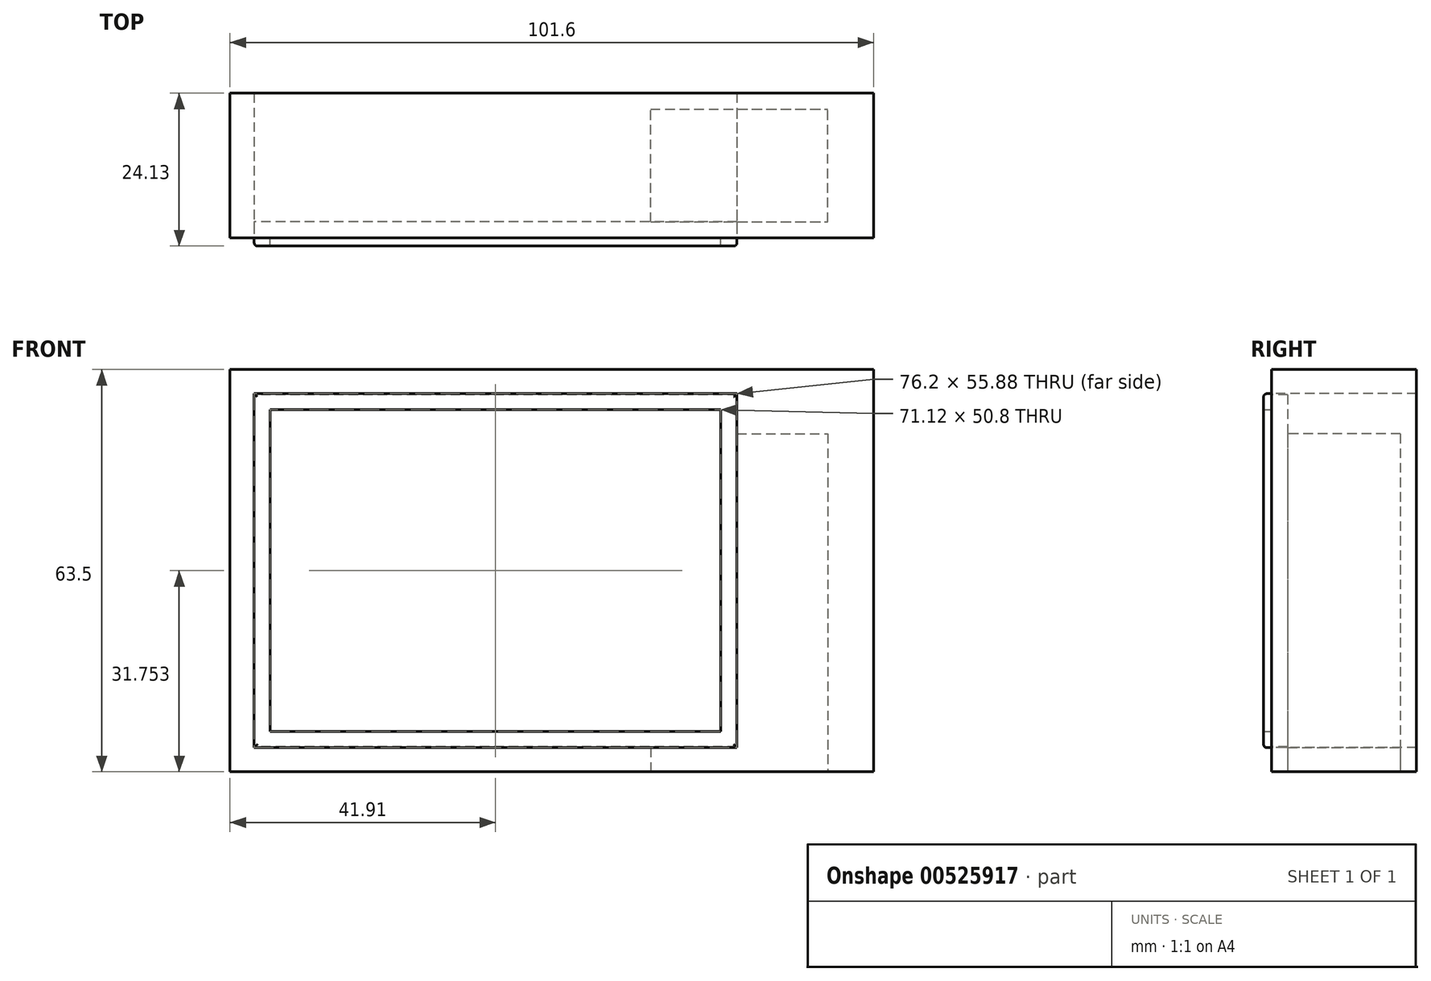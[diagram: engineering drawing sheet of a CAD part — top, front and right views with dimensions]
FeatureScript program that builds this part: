
annotation { "Feature Type Name" : "Feature", "Feature Type Description" : "" }
export const myFeature = defineFeature(function(context is Context, id is Id, definition is map)
    precondition{}
    {
        {
            var Q0;
            Q0=qCreatedBy(makeId("Front.planeOp"),FACE);
            var sketch = newSketch(context, id + "F0", { "sketchPlane" : qUnion([Q0])});
            skLineSegment(sketch, "E0.bottom", {"start": v(-51.46, 25.97) * mm, "end": v(50.14, 25.97) * mm});
            skLineSegment(sketch, "E0.top", {"start": v(-51.46, -37.53) * mm, "end": v(50.14, -37.53) * mm});
            skLineSegment(sketch, "E0.left", {"start": v(-51.46, 25.97) * mm, "end": v(-51.46, -37.53) * mm});
            skLineSegment(sketch, "E0.right", {"start": v(50.14, 25.97) * mm, "end": v(50.14, -37.53) * mm});
            skLineSegment(sketch, "E1.bottom", {"start": v(-47.65, 22.16) * mm, "end": v(28.55, 22.16) * mm});
            skLineSegment(sketch, "E1.top", {"start": v(-47.65, -33.72) * mm, "end": v(28.55, -33.72) * mm});
            skLineSegment(sketch, "E1.left", {"start": v(-47.65, 22.16) * mm, "end": v(-47.65, -33.72) * mm});
            skLineSegment(sketch, "E1.right", {"start": v(28.55, 22.16) * mm, "end": v(28.55, -33.72) * mm});
            skLineSegment(sketch, "E2.bottom", {"start": v(-45.11, 19.62) * mm, "end": v(26, 19.62) * mm});
            skLineSegment(sketch, "E2.top", {"start": v(-45.11, -31.18) * mm, "end": v(26, -31.18) * mm});
            skLineSegment(sketch, "E2.left", {"start": v(-45.11, 19.62) * mm, "end": v(-45.11, -31.18) * mm});
            skLineSegment(sketch, "E2.right", {"start": v(26, 19.62) * mm, "end": v(26, -31.18) * mm});
            skSolve(sketch);
        }
        {
            var Q0;
            Q0=makeQuery(id+"F0.imprint","IMPRINT",FACE,{"disambiguationData":[TD([[makeQuery(id+"F0.imprint","IMPRINT",EDGE,{"derivedFrom":sQuery(id+"F0.wireOp",EDGE,"E1.bottom")}),-1.0]])]});
            extrude(context, id + "F1", {"entities" : qUnion([Q0]), "depth" : 1.27 * mm, "offsetDistance" : 25.4 * mm});
        }
        {
            var Q0;
            Q0=makeQuery(id+"F1.opExtrude","CAP_EDGE",EDGE,{"disambiguationData":[OSD([sQuery(id+"F0.wireOp",EDGE,"E1.right")])],"isStart":false});
            var Q1;
            Q1=makeQuery(id+"F1.opExtrude","CAP_EDGE",EDGE,{"disambiguationData":[OSD([sQuery(id+"F0.wireOp",EDGE,"E1.bottom")])],"isStart":false});
            var Q2;
            Q2=makeQuery(id+"F1.opExtrude","CAP_EDGE",EDGE,{"disambiguationData":[OSD([sQuery(id+"F0.wireOp",EDGE,"E1.top")])],"isStart":false});
            var Q3;
            Q3=makeQuery(id+"F1.opExtrude","CAP_EDGE",EDGE,{"disambiguationData":[OSD([sQuery(id+"F0.wireOp",EDGE,"E1.left")])],"isStart":false});
            fillet(context, id + "F2", {"entities" : qUnion([Q0, Q1, Q2, Q3]), "radius" : 0.5 * mm, "tangentPropagation" : true, "allowEdgeOverflow" : false});
        }
        {
            var Q0;
            Q0=makeQuery(id+"F0.imprint","IMPRINT",FACE,{"disambiguationData":[TD([[makeQuery(id+"F0.imprint","IMPRINT",EDGE,{"derivedFrom":sQuery(id+"F0.wireOp",EDGE,"E0.bottom")}),-1.0]])]});
            extrude(context, id + "F3", {"entities" : qUnion([Q0]), "oppositeDirection" : true, "depth" : 22.86 * mm, "offsetDistance" : 25.4 * mm});
        }
        {
            var Q0;
            Q0=makeQuery(id+"F0.imprint","IMPRINT",FACE,{"disambiguationData":[TD([[makeQuery(id+"F0.imprint","IMPRINT",EDGE,{"derivedFrom":sQuery(id+"F0.wireOp",EDGE,"E0.bottom")}),-1.0]])]});
            var sketch = newSketch(context, id + "F4", { "sketchPlane" : qUnion([Q0])});
            skLineSegment(sketch, "E3.bottom", {"start": v(28.57, 21.99) * mm, "end": v(-47.85, 21.99) * mm});
            skLineSegment(sketch, "E3.top", {"start": v(28.57, -33.59) * mm, "end": v(-47.85, -33.59) * mm});
            skLineSegment(sketch, "E3.left", {"start": v(28.57, 21.99) * mm, "end": v(28.57, -33.59) * mm});
            skLineSegment(sketch, "E3.right", {"start": v(-47.85, 21.99) * mm, "end": v(-47.85, -33.59) * mm});
            skSolve(sketch);
        }
        {
            var Q0;
            {var subQ0=sQuery(id+"F4.wireOp",EDGE,"E3.bottom");var subQ1=makeQuery(id+"F0.imprint","IMPRINT",EDGE,{"derivedFrom":sQuery(id+"F0.wireOp",EDGE,"E1.right")});var subQ2=makeQuery(id+"F4.imprint","INTERSECT",VERTEX,{"derivedFrom":[subQ1,subQ0]});Q0=makeQuery(id+"F4.imprint","IMPRINT",FACE,{"disambiguationData":[TD([[makeQuery(id+"F4.imprint","IMPRINT",EDGE,{"disambiguationData":[TD([[subQ2,-1.0]])],"derivedFrom":subQ0}),1.0]])]});}
            extrude(context, id + "F5", {"entities" : qUnion([Q0]), "oppositeDirection" : true, "depth" : 2.54 * mm, "offsetDistance" : 25.4 * mm});
        }
        {
            var Q0;
            Q0=makeQuery(id+"F3.opExtrude","SWEPT_FACE",FACE,{"disambiguationData":[OSD([sQuery(id+"F0.wireOp",EDGE,"E0.top")])]});
            var sketch = newSketch(context, id + "F6", { "sketchPlane" : qUnion([Q0])});
            skLineSegment(sketch, "E4.bottom", {"start": v(14.92, -2.54) * mm, "end": v(42.86, -2.54) * mm});
            skLineSegment(sketch, "E4.top", {"start": v(14.92, -20.32) * mm, "end": v(42.86, -20.32) * mm});
            skLineSegment(sketch, "E4.left", {"start": v(14.92, -2.54) * mm, "end": v(14.92, -20.32) * mm});
            skLineSegment(sketch, "E4.right", {"start": v(42.86, -2.54) * mm, "end": v(42.86, -20.32) * mm});
            skSolve(sketch);
        }
        {
            var Q0;
            Q0=makeQuery(id+"F6.imprint","IMPRINT",FACE,{"disambiguationData":[TD([[makeQuery(id+"F6.imprint","IMPRINT",EDGE,{"derivedFrom":sQuery(id+"F6.wireOp",EDGE,"E4.bottom")}),-1.0]])]});
            extrude(context, id + "F7", {"entities" : qUnion([Q0]), "operationType" : NewBodyOperationType.REMOVE, "oppositeDirection" : true, "depth" : 53.34 * mm, "offsetDistance" : 25.4 * mm});
        }
    });
